FCSTD DOCUMENT  (FreeCAD 0.17R13509 (Git))
Label: eskutoidea2ertzakkoloreak
License: All rights reserved
LicenseURL: http://en.wikipedia.org/wiki/All_rights_reserved
objects: Part::Feature×11, Sketcher::SketchObject×3, Part::Part2DObjectPython×3, PartDesign::Body×1
note: 18 computed .brp shape members not serialized (recipe doc carries the construction recipe); baked Part::Feature solids carry a one-line shape summary decoded from their .brp

FEATURE [Sketcher::SketchObject] Sketch  label="Behekoaurpegia"
  MapMode = 5
  Support = -> [XY_Plane]
  sketch-geometry (13):
    g0: LineSegment StartX=20 StartY=27.5276 StartZ=0 EndX=-20 EndY=27.5276 EndZ=0
    g1: LineSegment StartX=-20 StartY=27.5276 StartZ=0 EndX=-32.3607 EndY=-10.5146 EndZ=0
    g2: LineSegment StartX=-32.3607 StartY=-10.5146 StartZ=0 EndX=0 EndY=-34.026 EndZ=0
    g3: LineSegment StartX=0 StartY=-34.026 StartZ=0 EndX=32.3607 EndY=-10.5146 EndZ=0
    g4: LineSegment StartX=32.3607 StartY=-10.5146 StartZ=0 EndX=20 EndY=27.5276 EndZ=0
    g5: Circle [constr] CenterX=0 CenterY=0 CenterZ=0 NormalX=0 NormalY=0 NormalZ=1 AngleXU=0 Radius=34.026
    g6: LineSegment StartX=20 StartY=27.5276 StartZ=0 EndX=40 EndY=62.1687 EndZ=0
    g7: LineSegment StartX=40 StartY=62.1687 StartZ=0 EndX=20 EndY=96.8097 EndZ=0
    g8: LineSegment StartX=20 StartY=96.8097 StartZ=0 EndX=-20 EndY=96.8097 EndZ=0
    g9: LineSegment StartX=-20 StartY=96.8097 StartZ=0 EndX=-40 EndY=62.1687 EndZ=0
    g10: LineSegment StartX=-40 StartY=62.1687 StartZ=0 EndX=-20 EndY=27.5276 EndZ=0
    g11: LineSegment StartX=-20 StartY=27.5276 StartZ=0 EndX=20 EndY=27.5276 EndZ=0
    g12: Circle [constr] CenterX=0 CenterY=62.1687 CenterZ=0 NormalX=0 NormalY=0 NormalZ=1 AngleXU=0 Radius=40
  constraints (29):
    c: Coincident(g0,g1)
    c: Coincident(g1,g2)
    c: Coincident(g2,g3)
    c: Coincident(g3,g4)
    c: Coincident(g4,g0)
    c: Equal(g0, g1-g4) x4
    c: PointOnObject(g0,g5)
    c: PointOnObject(g1,g5)
    c: PointOnObject(g2,g5)
    c: PointOnObject(g3,g5)
    c: PointOnObject(g4,g5)
    c: DistanceX(g0,g0) = 40
    c: Coincident(g6,g7)
    c: Coincident(g7,g8)
    c: Coincident(g8,g9)
    c: Coincident(g9,g10)
    c: Coincident(g10,g11)
    c: Coincident(g11,g6)
    c: Equal(g6, g7-g11) x5
    c: PointOnObject(g6,g12)
    c: PointOnObject(g7,g12)
    c: PointOnObject(g8,g12)
    c: PointOnObject(g9,g12)
    c: PointOnObject(g10,g12)
    c: PointOnObject(g11,g12)
    c: Coincident(g10,g0)
    c: Coincident(g6,g0)
    c: Symmetric(g0,g0,g-2)
    c: Coincident(g5,g-1)
FEATURE [Sketcher::SketchObject] Sketch001  label="Goikoaurpegia"
  AttachmentOffset = pos=(0,0,100) rot=(0,0,1;0rad)
  ExternalGeometry = -> [Sketch]
  MapMode = 5
  Placement = pos=(0,0,100) rot=(0,0,1;0rad)
  Support = -> [XY_Plane]
  sketch-geometry (13):
    g0: LineSegment StartX=20 StartY=-41.7544 StartZ=0 EndX=40 EndY=-7.11338 EndZ=0
    g1: LineSegment StartX=40 StartY=-7.11338 StartZ=0 EndX=20 EndY=27.5276 EndZ=0
    g2: LineSegment StartX=20 StartY=27.5276 StartZ=0 EndX=-20 EndY=27.5276 EndZ=0
    g3: LineSegment StartX=-20 StartY=27.5276 StartZ=0 EndX=-40 EndY=-7.11338 EndZ=0
    g4: LineSegment StartX=-40 StartY=-7.11338 StartZ=0 EndX=-20 EndY=-41.7544 EndZ=0
    g5: LineSegment StartX=-20 StartY=-41.7544 StartZ=0 EndX=20 EndY=-41.7544 EndZ=0
    g6: Circle [constr] CenterX=0 CenterY=-7.11338 CenterZ=0 NormalX=0 NormalY=0 NormalZ=1 AngleXU=0 Radius=40
    g7: LineSegment StartX=20 StartY=27.5276 StartZ=0 EndX=32.3607 EndY=65.5699 EndZ=0
    g8: LineSegment StartX=32.3607 StartY=65.5699 StartZ=0 EndX=-2.3e-11 EndY=89.0813 EndZ=0
    g9: LineSegment StartX=-2.3e-11 StartY=89.0813 StartZ=0 EndX=-32.3607 EndY=65.5699 EndZ=0
    g10: LineSegment StartX=-32.3607 StartY=65.5699 StartZ=0 EndX=-20 EndY=27.5276 EndZ=0
    g11: LineSegment StartX=-20 StartY=27.5276 StartZ=0 EndX=20 EndY=27.5276 EndZ=0
    g12: Circle [constr] CenterX=-5e-12 CenterY=55.0553 CenterZ=0 NormalX=0 NormalY=0 NormalZ=1 AngleXU=0 Radius=34.026
  constraints (28):
    c: Coincident(g0,g1)
    c: Coincident(g1,g2)
    c: Coincident(g2,g3)
    c: Coincident(g3,g4)
    c: Coincident(g4,g5)
    c: Coincident(g5,g0)
    c: Equal(g0, g1-g5) x5
    c: PointOnObject(g0,g6)
    c: PointOnObject(g1,g6)
    c: PointOnObject(g2,g6)
    c: PointOnObject(g3,g6)
    c: PointOnObject(g4,g6)
    c: PointOnObject(g5,g6)
    c: Coincident(g2,g-3)
    c: Coincident(g1,g-3)
    c: Coincident(g7,g8)
    c: Coincident(g8,g9)
    c: Coincident(g9,g10)
    c: Coincident(g10,g11)
    c: Coincident(g11,g7)
    c: Equal(g7, g8-g11) x4
    c: PointOnObject(g7,g12)
    c: PointOnObject(g8,g12)
    c: PointOnObject(g9,g12)
    c: PointOnObject(g10,g12)
    c: PointOnObject(g11,g12)
    c: Coincident(g10,g2)
    c: Coincident(g7,g1)
FEATURE [Sketcher::SketchObject] Sketch002  label="Erdikoerpina"
  AttachmentOffset = pos=(0,0,50) rot=(0,0,1;0rad)
  ExternalGeometry = -> [Sketch,Sketch001]
  MapMode = 5
  Placement = pos=(0,0,50) rot=(0,0,1;0rad)
  Support = -> [XY_Plane]
  sketch-geometry (4):
    g0: LineSegment StartX=20 StartY=27.5155 StartZ=0 EndX=30 EndY=44.836 EndZ=0
    g1: LineSegment StartX=20 StartY=27.5155 StartZ=0 EndX=30 EndY=10.195 EndZ=0
    g2: LineSegment StartX=30 StartY=44.836 StartZ=0 EndX=30 EndY=10.195 EndZ=0
    g3: LineSegment StartX=20 StartY=27.5155 StartZ=0 EndX=30 EndY=27.5155 EndZ=0
  constraints (12):
    c: Coincident(g1,g0)
    c: Parallel(g0,g-3)
    c: Parallel(g-4,g1)
    c: Distance(g0) = 20
    c: Equal(g1,g0)
    c: Coincident(g2,g0)
    c: Vertical(g2)
    c: PointOnObject(g3,g2)
    c: Horizontal(g3)
    c: Coincident(g0,g3)
    c: Coincident(g2,g1)
    c: DistanceX(g-1,g0) = 20
FEATURE [PartDesign::Body] Body
  Group = -> [Sketch,Sketch001,Sketch002]
  Origin = -> Origin
FEATURE [Part::Feature] Edge
  shape: bbox 20 x 7.728 x 100 mm, 0 faces, 0 solids (baked)
FEATURE [Part::Feature] Edge001
  shape: bbox 7.639 x 3.401 x 100 mm, 0 faces, 0 solids (baked)
FEATURE [Part::Feature] Edge002
  shape: bbox 12.36 x 31.24 x 100 mm, 0 faces, 0 solids (baked)
FEATURE [Part::Feature] Edge003
  shape: bbox 2e-07 x 2e-07 x 100 mm, 0 faces, 0 solids (baked)
FEATURE [Part::Feature] Edge004
  shape: bbox 10 x 0.01215 x 50 mm, 0 faces, 0 solids (baked)
FEATURE [Part::Feature] Edge005
  shape: bbox 10 x 34.63 x 50 mm, 0 faces, 0 solids (baked)
FEATURE [Part::Feature] Edge006
  shape: bbox 10 x 0.01215 x 50 mm, 0 faces, 0 solids (baked)
FEATURE [Part::Feature] Edge007
  shape: bbox 10 x 34.65 x 50 mm, 0 faces, 0 solids (baked)
FEATURE [Part::Feature] Edge008
  shape: bbox 7.639 x 3.401 x 100 mm, 0 faces, 0 solids (baked)
FEATURE [Part::Feature] Edge009
  shape: bbox 20 x 7.728 x 100 mm, 0 faces, 0 solids (baked)
FEATURE [Part::Feature] Edge010
  shape: bbox 12.36 x 31.24 x 100 mm, 0 faces, 0 solids (baked)
FEATURE [Part::Part2DObjectPython] Line001  # Draft 2D object (typed FeaturePython)
  ChamferSize = 0
  Closed = false
  End = (30,44.836,50)
  FilletRadius = 0
  Length = 50.0021
  MakeFace = false
  Points = (2) [(30.2249,45.2377,0),(30,44.836,50)]
  Start = (30.2249,45.2377,0)
  Subdivisions = 0
FEATURE [Part::Part2DObjectPython] Line  # Draft 2D object (typed FeaturePython)
  ChamferSize = 0
  Closed = false
  End = (30,10.195,50)
  FilletRadius = 0
  Length = 50.0467
  MakeFace = false
  Points = (2) [(28.9242,12.0705,100),(30,10.195,50)]
  Start = (28.9242,12.0705,100)
  Subdivisions = 0
FEATURE [Part::Part2DObjectPython] Line002  # Draft 2D object (typed FeaturePython)
  ChamferSize = 0
  Closed = false
  End = (20.0183,27.5155,50)
  FilletRadius = 0
  Length = 50
  MakeFace = false
  Points = (2) [(20,27.5276,100),(20.0183,27.5155,50)]
  Start = (20,27.5276,100)
  Subdivisions = 0
